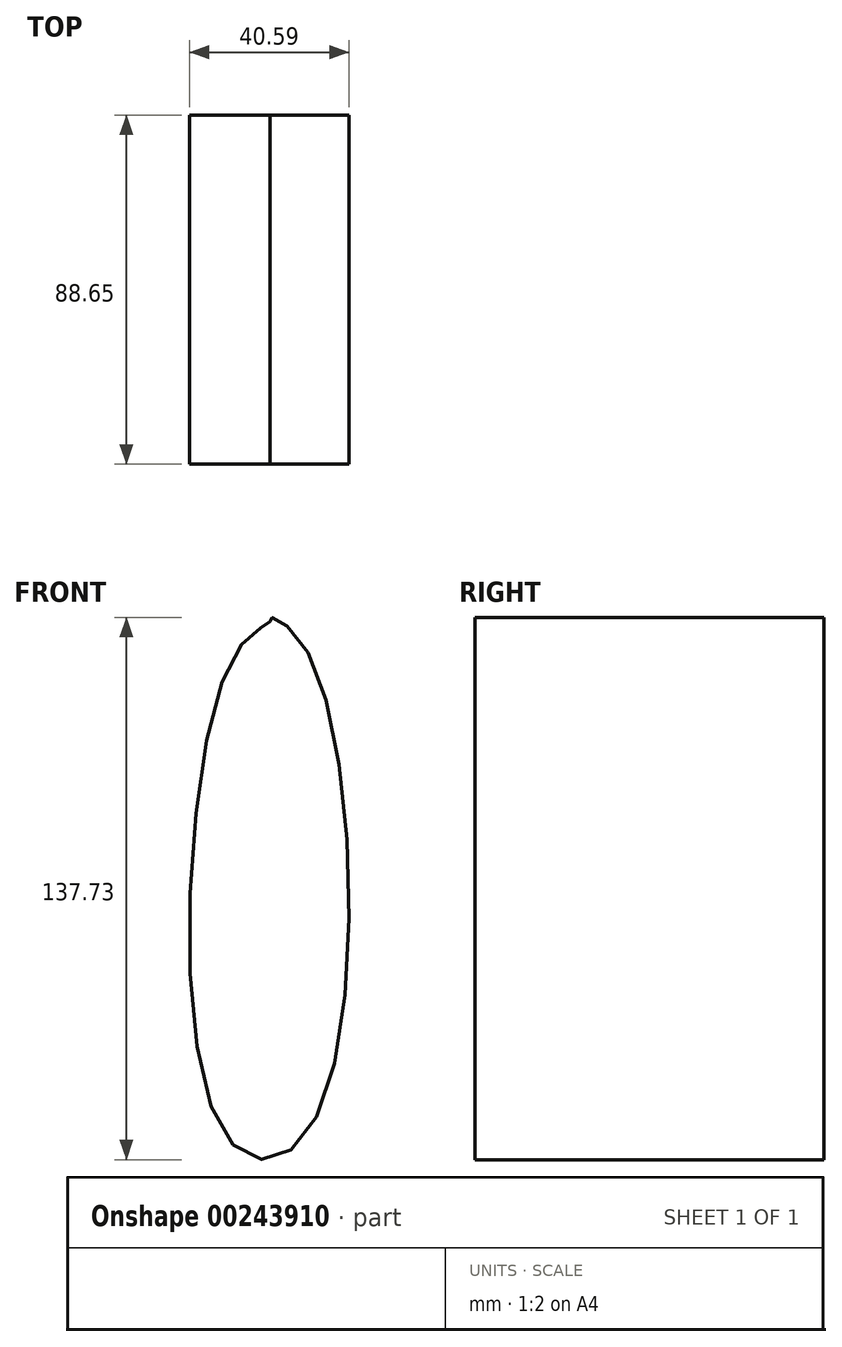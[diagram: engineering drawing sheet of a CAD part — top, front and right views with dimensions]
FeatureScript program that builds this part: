
annotation { "Feature Type Name" : "Feature", "Feature Type Description" : "" }
export const myFeature = defineFeature(function(context is Context, id is Id, definition is map)
    precondition{}
    {
        {
            var Q0;
            Q0=qCreatedBy(makeId("Front.planeOp"),FACE);
            var sketch = newSketch(context, id + "F0", { "sketchPlane" : qUnion([Q0])});
            skFitSpline(sketch, "E0", {"points": [v(9.62, 46.56) * mm, v(0, 55.3) * mm, v(0, 54.43) * mm, v(-8.74, 46.56) * mm, v(-11.8, -75.41) * mm, v(10.05, -74.54) * mm, v(9.62, 46.56) * mm]});
            skSolve(sketch);
        }
        {
            var Q0;
            Q0=makeQuery(id+"F0.imprint","IMPRINT",FACE,{"disambiguationData":[TD([[makeQuery(id+"F0.imprint","IMPRINT",EDGE,{"derivedFrom":sQuery(id+"F0.wireOp",EDGE,"E0")}),1.0]])]});
            extrude(context, id + "F1", {"entities" : qUnion([Q0]), "depth" : 88.65 * mm});
        }
    });
